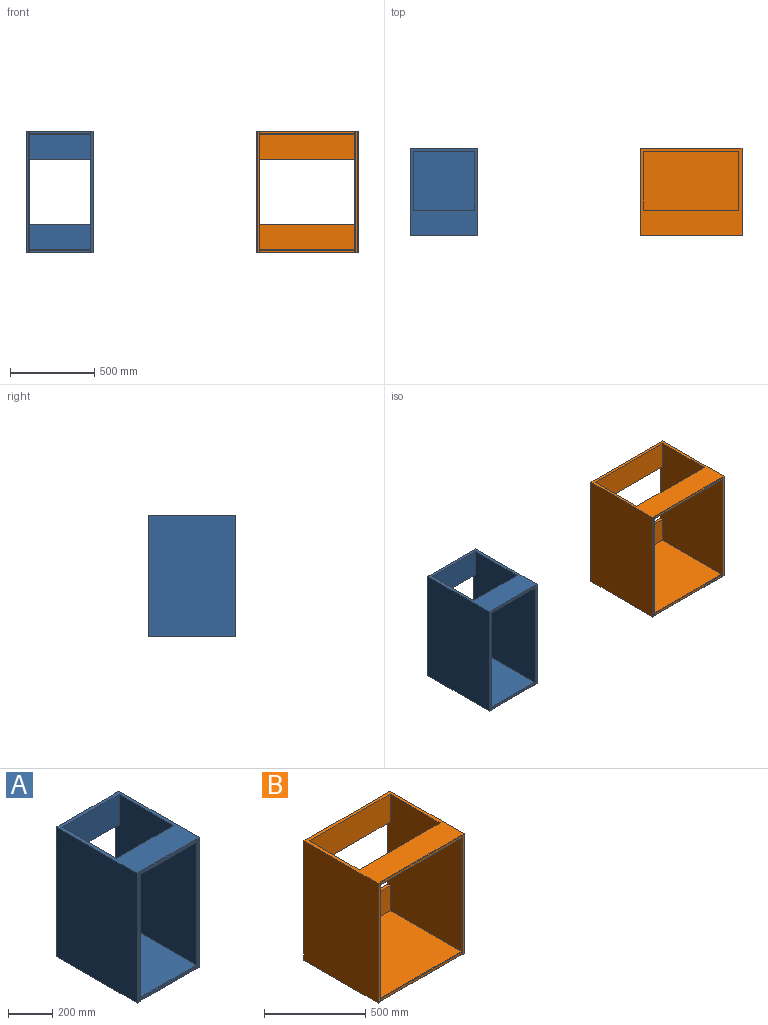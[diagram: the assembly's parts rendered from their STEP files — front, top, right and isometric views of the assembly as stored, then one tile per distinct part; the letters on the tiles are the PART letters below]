
ASSEMBLY  parts=2 mates=1
PART A: 33 faces, bbox 400x520x720 mm
  f0: plane 2x2mm, normal (-1,0,0), area 0.9mm2, adj f11,f25,f32
  f1: plane 720x518mm, normal (-1,0,0), area 355249.7mm2, adj f4,f6,f8,f9,f11,f18,f19,f20
  f2: plane 2x2mm, normal (1,0,0), area 0.9mm2, adj f9,f28,f29
  f3: plane 720x518mm, normal (1,0,0), area 355249.7mm2, adj f4,f6,f7,f9,f11,f18,f19,f20
  f4: plane 496x364mm, normal (0,0,1), area 180544mm2, adj f1,f3,f24,f26
  f5: plane 2x2mm, normal (-1,0,0), area 0.9mm2, adj f9,f28,f32
  f6: plane 364x148mm, normal (0,0,-1), area 53872mm2, adj f1,f3,f21,f27
  f7: plane 720x18mm, normal (0,1,0), area 12960mm2, adj f3,f9,f11,f14
  f8: plane 720x18mm, normal (0,1,0), area 12960mm2, adj f1,f9,f11,f12
  f9: plane 520x400mm, normal (0,0,1), area 79140.6mm2, adj f1,f2,f3,f5,f7,f8,f10,f12
  f10: plane 720x14mm, normal (0,-1,0), area 10080mm2, adj f9,f11,f29,f30
  f11: plane 520x400mm, normal (0,0,-1), area 205812.6mm2, adj f0,f1,f3,f7,f8,f10,f12,f13
  f12: plane 720x518mm, normal (1,0,0), area 372960mm2, adj f8,f9,f11,f31
  f13: plane 2x2mm, normal (1,0,0), area 0.9mm2, adj f11,f25,f29
  f14: plane 720x518mm, normal (-1,0,0), area 372960mm2, adj f7,f9,f11,f30
  f15: plane 720x14mm, normal (0,-1,0), area 10080mm2, adj f9,f11,f31,f32
  f16: plane 364x14mm, normal (0,-1,0), area 5096mm2, adj f27,f28,f29,f32
  f17: plane 364x14mm, normal (0,-1,0), area 5096mm2, adj f25,f26,f29,f32
  f18: plane 364x168mm, normal (0,1,0), area 61152mm2, adj f1,f3,f11,f23
  f19: plane 364x168mm, normal (0,1,0), area 61152mm2, adj f1,f3,f9,f22
  f20: plane 364x168mm, normal (0,-1,0), area 61152mm2, adj f1,f3,f9,f22
  f21: plane 364x18mm, normal (0,1,0), area 6552mm2, adj f1,f3,f6,f9
  f22: plane 364x18mm, normal (0,0,-1), area 6552mm2, adj f1,f3,f19,f20
  f23: plane 364x18mm, normal (0,0,1), area 6552mm2, adj f1,f3,f18,f24
  f24: plane 364x150mm, normal (0,-1,0), area 54600mm2, adj f1,f3,f4,f23
  f25: cylinder r=2mm len=364mm, axis (1,0,0), area 1143.5mm2, adj f0,f11,f13,f17
  f26: cylinder r=2mm len=364mm, axis (-1,0,0), area 1143.5mm2, adj f1,f3,f4,f17
  f27: cylinder r=2mm len=364mm, axis (1,0,0), area 1143.5mm2, adj f1,f3,f6,f16
  f28: cylinder r=2mm len=364mm, axis (-1,0,0), area 1143.5mm2, adj f2,f5,f9,f16
  f29: cylinder r=2mm len=720mm, axis (0,0,1), area 2261.9mm2, adj f2,f3,f9,f10,f11,f13,f16,f17
  f30: cylinder r=2mm len=720mm, axis (0,0,-1), area 2261.9mm2, adj f9,f10,f11,f14
  f31: cylinder r=2mm len=720mm, axis (0,0,1), area 2261.9mm2, adj f9,f11,f12,f15
  f32: cylinder r=2mm len=720mm, axis (0,0,-1), area 2261.9mm2, adj f0,f1,f5,f9,f11,f15,f16,f17
PART B: 33 faces, bbox 600x520x720 mm
  f0: plane 2x2mm, normal (-1,0,0), area 0.9mm2, adj f11,f25,f32
  f1: plane 720x518mm, normal (-1,0,0), area 355249.7mm2, adj f4,f6,f8,f9,f11,f18,f19,f20
  f2: plane 2x2mm, normal (1,0,0), area 0.9mm2, adj f9,f28,f29
  f3: plane 720x518mm, normal (1,0,0), area 355249.7mm2, adj f4,f6,f7,f9,f11,f18,f19,f20
  f4: plane 564x496mm, normal (0,0,1), area 279744mm2, adj f1,f3,f24,f26
  f5: plane 2x2mm, normal (-1,0,0), area 0.9mm2, adj f9,f28,f32
  f6: plane 564x148mm, normal (0,0,-1), area 83472mm2, adj f1,f3,f21,f27
  f7: plane 720x18mm, normal (0,1,0), area 12960mm2, adj f3,f9,f11,f14
  f8: plane 720x18mm, normal (0,1,0), area 12960mm2, adj f1,f9,f11,f12
  f9: plane 600x520mm, normal (0,0,1), area 112340.6mm2, adj f1,f2,f3,f5,f7,f8,f10,f12
  f10: plane 720x14mm, normal (0,-1,0), area 10080mm2, adj f9,f11,f29,f30
  f11: plane 600x520mm, normal (0,0,-1), area 308612.6mm2, adj f0,f1,f3,f7,f8,f10,f12,f13
  f12: plane 720x518mm, normal (1,0,0), area 372960mm2, adj f8,f9,f11,f31
  f13: plane 2x2mm, normal (1,0,0), area 0.9mm2, adj f11,f25,f29
  f14: plane 720x518mm, normal (-1,0,0), area 372960mm2, adj f7,f9,f11,f30
  f15: plane 720x14mm, normal (0,-1,0), area 10080mm2, adj f9,f11,f31,f32
  f16: plane 564x14mm, normal (0,-1,0), area 7896mm2, adj f27,f28,f29,f32
  f17: plane 564x14mm, normal (0,-1,0), area 7896mm2, adj f25,f26,f29,f32
  f18: plane 564x168mm, normal (0,1,0), area 94752mm2, adj f1,f3,f11,f23
  f19: plane 564x168mm, normal (0,1,0), area 94752mm2, adj f1,f3,f9,f22
  f20: plane 564x168mm, normal (0,-1,0), area 94752mm2, adj f1,f3,f9,f22
  f21: plane 564x18mm, normal (0,1,0), area 10152mm2, adj f1,f3,f6,f9
  f22: plane 564x18mm, normal (0,0,-1), area 10152mm2, adj f1,f3,f19,f20
  f23: plane 564x18mm, normal (0,0,1), area 10152mm2, adj f1,f3,f18,f24
  f24: plane 564x150mm, normal (0,-1,0), area 84600mm2, adj f1,f3,f4,f23
  f25: cylinder r=2mm len=564mm, axis (1,0,0), area 1771.9mm2, adj f0,f11,f13,f17
  f26: cylinder r=2mm len=564mm, axis (-1,0,0), area 1771.9mm2, adj f1,f3,f4,f17
  f27: cylinder r=2mm len=564mm, axis (1,0,0), area 1771.9mm2, adj f1,f3,f6,f16
  f28: cylinder r=2mm len=564mm, axis (-1,0,0), area 1771.9mm2, adj f2,f5,f9,f16
  f29: cylinder r=2mm len=720mm, axis (0,0,1), area 2261.9mm2, adj f2,f3,f9,f10,f11,f13,f16,f17
  f30: cylinder r=2mm len=720mm, axis (0,0,-1), area 2261.9mm2, adj f9,f10,f11,f14
  f31: cylinder r=2mm len=720mm, axis (0,0,1), area 2261.9mm2, adj f9,f11,f12,f15
  f32: cylinder r=2mm len=720mm, axis (0,0,-1), area 2261.9mm2, adj f0,f1,f5,f9,f11,f15,f16,f17
PLACE A t=(-1335.5,92.23,552.77)mm
PLACE B t=(132.5,92.23,552.77)mm
MATE parallel A.f12 <-> B.f14  axis (1,0,0) through (-1135.5,353.23,903.77)mm
